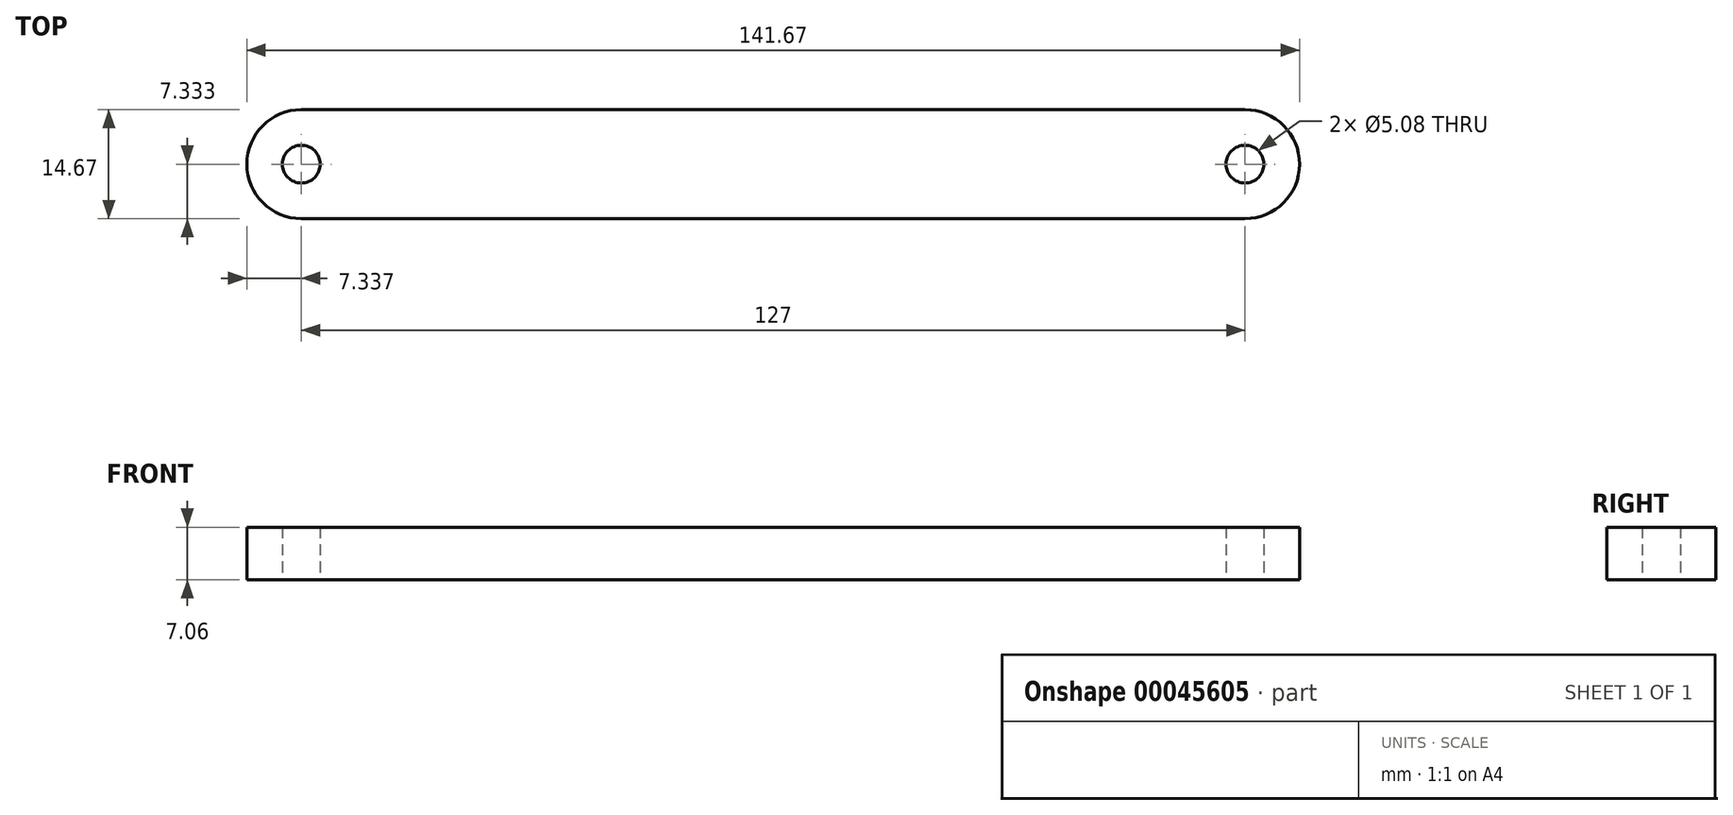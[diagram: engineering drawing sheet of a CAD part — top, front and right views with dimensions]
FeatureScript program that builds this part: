
annotation { "Feature Type Name" : "Feature", "Feature Type Description" : "" }
export const myFeature = defineFeature(function(context is Context, id is Id, definition is map)
    precondition{}
    {
        {
            var Q0;
            Q0=qCreatedBy(makeId("Top.planeOp"),FACE);
            var sketch = newSketch(context, id + "F0", { "sketchPlane" : qUnion([Q0])});
            skLineSegment(sketch, "E0.bottom", {"start": v(-34.23, 17.32) * mm, "end": v(92.77, 17.32) * mm});
            skLineSegment(sketch, "E0.top", {"start": v(-34.23, 2.65) * mm, "end": v(92.77, 2.65) * mm});
            skArc(sketch, "E1", {"start": v(-34.23, 17.32) * mm, "mid": v(-41.57, 9.98) * mm, "end": v(-34.23, 2.65) * mm});
            skArc(sketch, "E2", {"start": v(92.77, 2.65) * mm, "mid": v(100.1, 9.98) * mm, "end": v(92.77, 17.32) * mm});
            skCircle(sketch, "E3", {"center": v(-34.23, 9.98) * mm, "radius": 2.54 * mm});
            skCircle(sketch, "E4", {"center": v(92.77, 9.98) * mm, "radius": 2.54 * mm});
            skLineSegment(sketch, "E5", {"start": v(22.68, 2.65) * mm, "end": v(22.68, 17.32) * mm});
            skSolve(sketch);
        }
        {
            var Q0;
            Q0=qSketchRegion(id+"F0",true);
            extrude(context, id + "F1", {"entities" : qUnion([Q0]), "depth" : 7.06 * mm});
        }
    });
